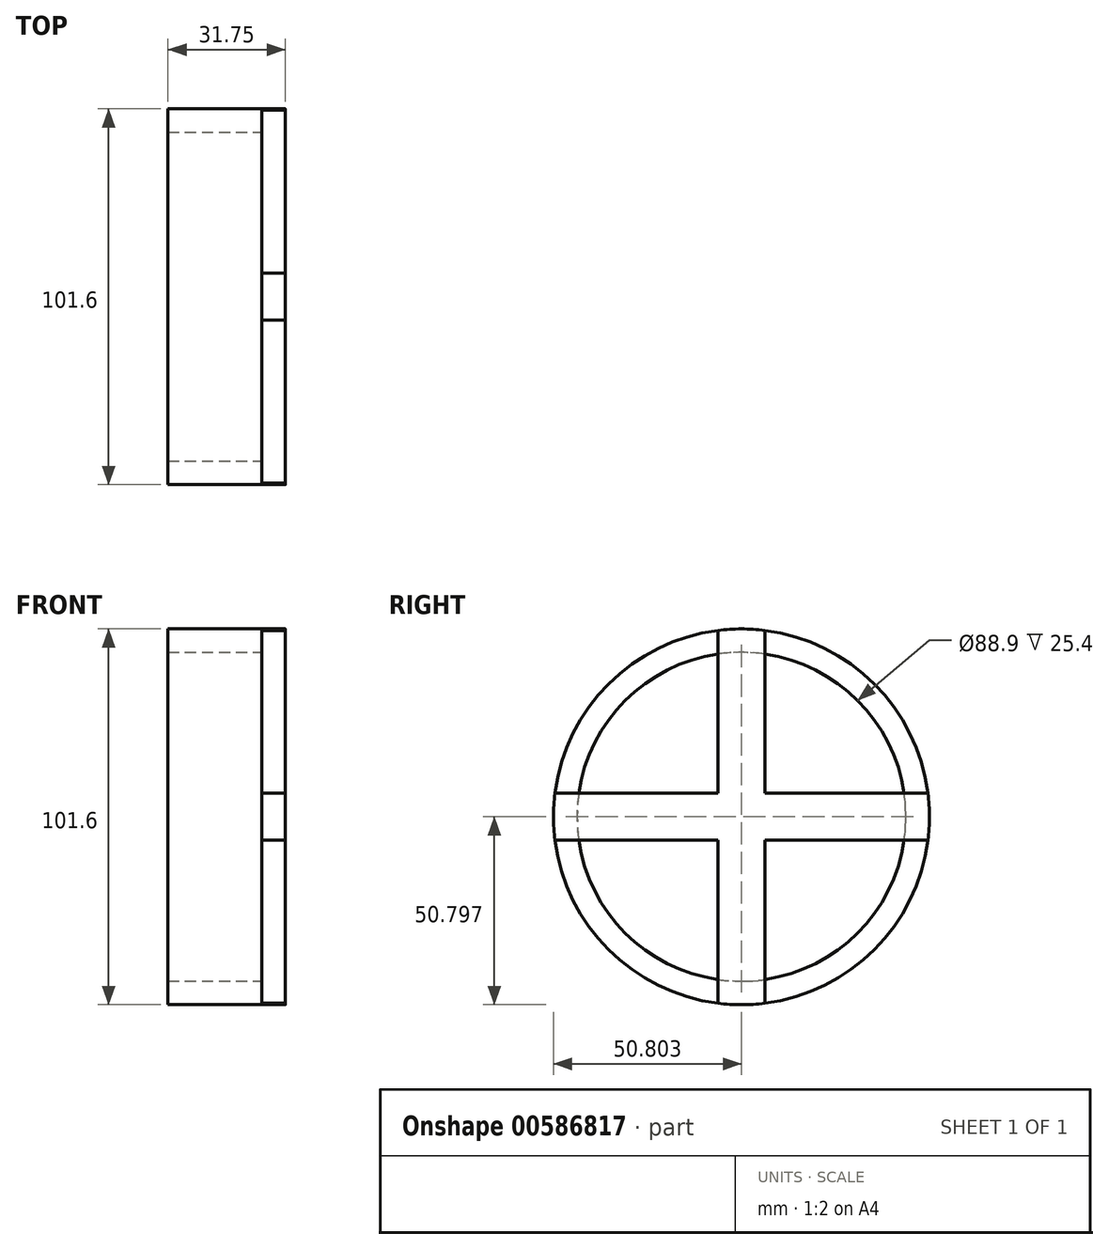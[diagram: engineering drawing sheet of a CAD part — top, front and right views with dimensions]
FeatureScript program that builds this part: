
annotation { "Feature Type Name" : "Feature", "Feature Type Description" : "" }
export const myFeature = defineFeature(function(context is Context, id is Id, definition is map)
    precondition{}
    {
        {
            var Q0;
            Q0=qCreatedBy(makeId("Right.planeOp"),FACE);
            var sketch = newSketch(context, id + "F0", { "sketchPlane" : qUnion([Q0])});
            skCircle(sketch, "E0", {"center": v(-11.94, 3.53) * mm, "radius": 50.8 * mm});
            skLineSegment(sketch, "E1", {"start": v(-18.29, 53.93) * mm, "end": v(-18.29, 9.88) * mm});
            skLineSegment(sketch, "E2", {"start": v(-18.29, -2.82) * mm, "end": v(-18.29, -46.87) * mm});
            skLineSegment(sketch, "E3", {"start": v(-5.59, 53.93) * mm, "end": v(-5.59, 9.88) * mm});
            skLineSegment(sketch, "E4", {"start": v(-5.59, -2.82) * mm, "end": v(-5.59, -46.87) * mm});
            skLineSegment(sketch, "E5", {"start": v(-18.29, 9.88) * mm, "end": v(-62.34, 9.88) * mm});
            skLineSegment(sketch, "E6", {"start": v(-5.59, 9.88) * mm, "end": v(38.46, 9.88) * mm});
            skLineSegment(sketch, "E7", {"start": v(-18.29, -2.82) * mm, "end": v(-62.34, -2.82) * mm});
            skLineSegment(sketch, "E8", {"start": v(-5.59, -2.82) * mm, "end": v(38.46, -2.82) * mm});
            skCircle(sketch, "E9", {"center": v(-11.94, 3.53) * mm, "radius": 44.45 * mm});
            skSolve(sketch);
        }
        {
            var Q0;
            {var subQ4=sQuery(id+"F0.wireOp",EDGE,"E1");Q0=makeQuery(id+"F0.imprint","IMPRINT",FACE,{"disambiguationData":[TD([[makeQuery(id+"F0.imprint","IMPRINT",EDGE,{"derivedFrom":subQ4}),1.0]])]});}
            var Q1;
            {var subQ9=sQuery(id+"F0.wireOp",EDGE,"E5");var subQ13=sQuery(id+"F0.wireOp",EDGE,"E1");var subQ14=makeQuery(id+"F0.imprint","INTERSECT",VERTEX,{"derivedFrom":[subQ13,subQ9]});Q1=makeQuery(id+"F0.imprint","IMPRINT",FACE,{"disambiguationData":[TD([[makeQuery(id+"F0.imprint","IMPRINT",EDGE,{"disambiguationData":[TD([[subQ14,1.0]])],"derivedFrom":subQ13}),1.0]])]});}
            var Q2;
            {var subQ0=sQuery(id+"F0.wireOp",EDGE,"E5");var subQ1=sQuery(id+"F0.wireOp",EDGE,"E0");var subQ2=makeQuery(id+"F0.imprint","INTERSECT",VERTEX,{"derivedFrom":[subQ1,subQ0]});Q2=makeQuery(id+"F0.imprint","IMPRINT",FACE,{"disambiguationData":[TD([[makeQuery(id+"F0.imprint","IMPRINT",EDGE,{"disambiguationData":[TD([[subQ2,-1.0]])],"derivedFrom":subQ1}),1.0]])]});}
            var Q3;
            {var subQ0=sQuery(id+"F0.wireOp",EDGE,"E6");var subQ1=sQuery(id+"F0.wireOp",EDGE,"E0");var subQ2=makeQuery(id+"F0.imprint","INTERSECT",VERTEX,{"derivedFrom":[subQ1,subQ0]});Q3=makeQuery(id+"F0.imprint","IMPRINT",FACE,{"disambiguationData":[TD([[makeQuery(id+"F0.imprint","IMPRINT",EDGE,{"disambiguationData":[TD([[subQ2,1.0]])],"derivedFrom":subQ1}),1.0]])]});}
            var Q4;
            {var subQ0=sQuery(id+"F0.wireOp",EDGE,"E2");var subQ1=sQuery(id+"F0.wireOp",EDGE,"E0");var subQ2=makeQuery(id+"F0.imprint","INTERSECT",VERTEX,{"derivedFrom":[subQ1,subQ0]});Q4=makeQuery(id+"F0.imprint","IMPRINT",FACE,{"disambiguationData":[TD([[makeQuery(id+"F0.imprint","IMPRINT",EDGE,{"disambiguationData":[TD([[subQ2,-1.0]])],"derivedFrom":subQ1}),1.0]])]});}
            extrude(context, id + "F1", {"entities" : qUnion([Q0, Q1, Q2, Q3, Q4]), "depth" : 6.35 * mm, "offsetDistance" : 25.4 * mm});
        }
        {
            var Q0;
            Q0 = qSketchRegion(id + "F0", true);
            extrude(context, id + "F2", {"entities" : qUnion([Q0]), "oppositeDirection" : true, "depth" : 25.4 * mm, "offsetDistance" : 25.4 * mm});
        }
    });
